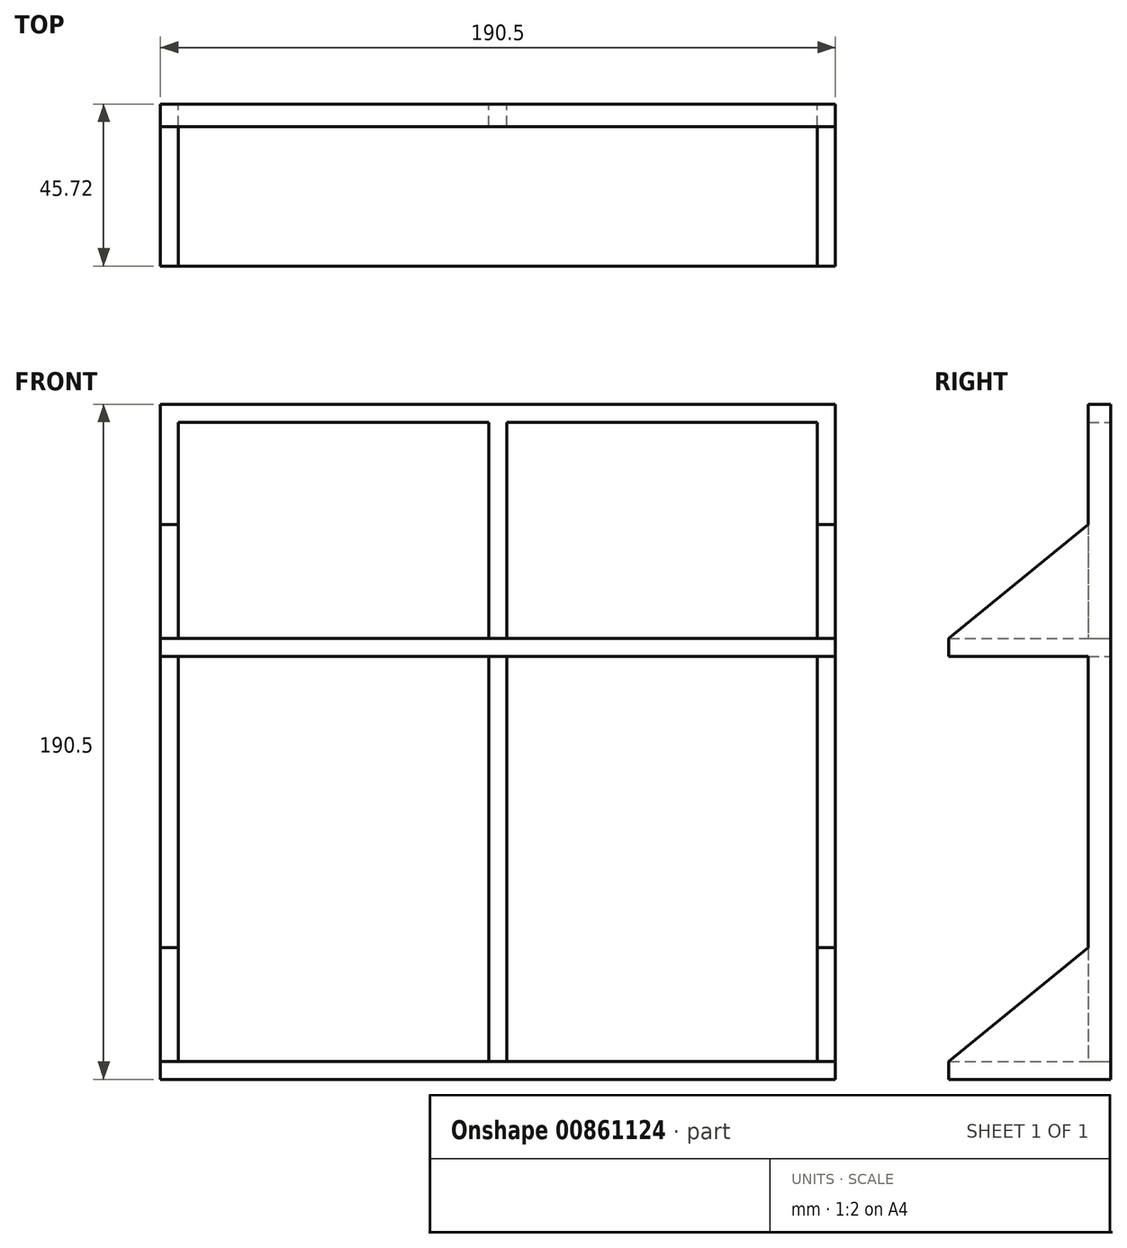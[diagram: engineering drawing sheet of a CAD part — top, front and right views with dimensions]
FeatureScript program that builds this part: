
annotation { "Feature Type Name" : "Feature", "Feature Type Description" : "" }
export const myFeature = defineFeature(function(context is Context, id is Id, definition is map)
    precondition{}
    {
        {
            var Q0;
            Q0=qCreatedBy(makeId("Front.planeOp"),FACE);
            var sketch = newSketch(context, id + "F0", { "sketchPlane" : qUnion([Q0])});
            skLineSegment(sketch, "E0.bottom", {"start": v(-95.25, 95.25) * mm, "end": v(95.25, 95.25) * mm});
            skLineSegment(sketch, "E0.top", {"start": v(-95.25, -95.25) * mm, "end": v(95.25, -95.25) * mm});
            skLineSegment(sketch, "E0.left", {"start": v(-95.25, 95.25) * mm, "end": v(-95.25, -95.25) * mm});
            skLineSegment(sketch, "E0.right", {"start": v(95.25, 95.25) * mm, "end": v(95.25, -95.25) * mm});
            skPoint(sketch, "E0.middle", {"position": v(0, 0) * mm});
            skLineSegment(sketch, "E1", {"start": v(90.17, 90.17) * mm, "end": v(2.54, 90.17) * mm});
            skLineSegment(sketch, "E2", {"start": v(-95.25, -90.17) * mm, "end": v(-2.54, -90.17) * mm});
            skLineSegment(sketch, "E3", {"start": v(-90.17, 90.17) * mm, "end": v(-90.17, 29.2) * mm});
            skLineSegment(sketch, "E4", {"start": v(90.17, 90.17) * mm, "end": v(90.17, 29.2) * mm});
            skLineSegment(sketch, "E5", {"start": v(-95.25, 24.13) * mm, "end": v(95.25, 24.13) * mm});
            skLineSegment(sketch, "E6", {"start": v(-95.25, 29.2) * mm, "end": v(95.25, 29.2) * mm});
            skPoint(sketch, "E7.orphan", {"position": v(-90.17, -95.25) * mm});
            skPoint(sketch, "E8.orphan", {"position": v(90.17, -95.25) * mm});
            skPoint(sketch, "E9.orphan", {"position": v(95.25, 90.17) * mm});
            skLineSegment(sketch, "E10.trimOffspring", {"start": v(90.17, 24.13) * mm, "end": v(90.17, -90.17) * mm});
            skLineSegment(sketch, "E11.trimOffspring", {"start": v(-90.17, 24.13) * mm, "end": v(-90.17, -90.17) * mm});
            skLineSegment(sketch, "E12", {"start": v(2.54, 90.17) * mm, "end": v(2.54, 29.2) * mm});
            skLineSegment(sketch, "E13", {"start": v(-2.54, 90.17) * mm, "end": v(-2.54, 29.2) * mm});
            skLineSegment(sketch, "E14.trimOffspring", {"start": v(2.54, -90.17) * mm, "end": v(95.25, -90.17) * mm});
            skPoint(sketch, "E15.orphan", {"position": v(0, -90.17) * mm});
            skLineSegment(sketch, "E16.trimOffspring", {"start": v(-2.54, 90.17) * mm, "end": v(-90.17, 90.17) * mm});
            skLineSegment(sketch, "E17.trimOffspring", {"start": v(2.54, 24.13) * mm, "end": v(2.54, -90.17) * mm});
            skLineSegment(sketch, "E18.trimOffspring", {"start": v(-2.54, 24.13) * mm, "end": v(-2.54, -90.17) * mm});
            skLineSegment(sketch, "E19", {"start": v(-2.54, -90.17) * mm, "end": v(2.54, -90.17) * mm});
            skPoint(sketch, "E20.start.orphan", {"position": v(0, 90.17) * mm});
            skSolve(sketch);
        }
        {
            var Q0;
            {var subQ4=sQuery(id+"F0.wireOp",EDGE,"E0.left");var subQ6=sQuery(id+"F0.wireOp",EDGE,"E5");var subQ12=makeQuery(id+"F0.imprint","INTERSECT",VERTEX,{"derivedFrom":[subQ4,subQ6]});Q0=makeQuery(id+"F0.imprint","IMPRINT",FACE,{"disambiguationData":[TD([[makeQuery(id+"F0.imprint","IMPRINT",EDGE,{"disambiguationData":[TD([[subQ12,1.0]])],"derivedFrom":subQ4}),1.0]])]});}
            var Q1;
            {var subQ1=sQuery(id+"F0.wireOp",EDGE,"E0.top");Q1=makeQuery(id+"F0.imprint","IMPRINT",FACE,{"disambiguationData":[TD([[makeQuery(id+"F0.imprint","IMPRINT",EDGE,{"derivedFrom":subQ1}),1.0]])]});}
            extrude(context, id + "F1", {"entities" : qUnion([Q0, Q1]), "depth" : 45.72 * mm, "offsetDistance" : 25.4 * mm});
        }
        {
            var Q0;
            {var subQ5=sQuery(id+"F0.wireOp",EDGE,"E11.trimOffspring");Q0=makeQuery(id+"F0.imprint","IMPRINT",FACE,{"disambiguationData":[TD([[makeQuery(id+"F0.imprint","IMPRINT",EDGE,{"derivedFrom":subQ5}),-1.0]])]});}
            var Q1;
            {var subQ7=sQuery(id+"F0.wireOp",EDGE,"E0.bottom");Q1=makeQuery(id+"F0.imprint","IMPRINT",FACE,{"disambiguationData":[TD([[makeQuery(id+"F0.imprint","IMPRINT",EDGE,{"derivedFrom":subQ7}),-1.0]])]});}
            var Q2;
            {var subQ0=sQuery(id+"F0.wireOp",EDGE,"E17.trimOffspring");Q2=makeQuery(id+"F0.imprint","IMPRINT",FACE,{"disambiguationData":[TD([[makeQuery(id+"F0.imprint","IMPRINT",EDGE,{"derivedFrom":subQ0}),-1.0]])]});}
            var Q3;
            {var subQ5=sQuery(id+"F0.wireOp",EDGE,"E10.trimOffspring");Q3=makeQuery(id+"F0.imprint","IMPRINT",FACE,{"disambiguationData":[TD([[makeQuery(id+"F0.imprint","IMPRINT",EDGE,{"derivedFrom":subQ5}),1.0]])]});}
            extrude(context, id + "F2", {"entities" : qUnion([Q0, Q1, Q2, Q3]), "depth" : 6.35 * mm, "offsetDistance" : 25.4 * mm});
        }
        {
            var Q0;
            Q0=makeQuery(id+"F1.opExtrude","SWEPT_BODY",BODY,{"disambiguationData":[OSD([sQuery(id+"F0.wireOp",EDGE,"E0.top"),sQuery(id+"F0.wireOp",EDGE,"E0.left"),sQuery(id+"F0.wireOp",EDGE,"E0.right"),sQuery(id+"F0.wireOp",EDGE,"E2"),sQuery(id+"F0.wireOp",EDGE,"E14.trimOffspring"),sQuery(id+"F0.wireOp",EDGE,"E19")])]});
            var Q1;
            Q1=makeQuery(id+"F1.opExtrude","SWEPT_BODY",BODY,{"disambiguationData":[OSD([sQuery(id+"F0.wireOp",EDGE,"E0.left"),sQuery(id+"F0.wireOp",EDGE,"E0.right"),sQuery(id+"F0.wireOp",EDGE,"E5"),sQuery(id+"F0.wireOp",EDGE,"E6")])]});
            var Q2;
            Q2=makeQuery(id+"F2.opExtrude","SWEPT_BODY",BODY,{"disambiguationData":[OSD([sQuery(id+"F0.wireOp",EDGE,"E0.bottom"),sQuery(id+"F0.wireOp",EDGE,"E0.left"),sQuery(id+"F0.wireOp",EDGE,"E0.right"),sQuery(id+"F0.wireOp",EDGE,"E1"),sQuery(id+"F0.wireOp",EDGE,"E3"),sQuery(id+"F0.wireOp",EDGE,"E4"),sQuery(id+"F0.wireOp",EDGE,"E6"),sQuery(id+"F0.wireOp",EDGE,"E12"),sQuery(id+"F0.wireOp",EDGE,"E13"),sQuery(id+"F0.wireOp",EDGE,"E16.trimOffspring")])]});
            var Q3;
            Q3=makeQuery(id+"F2.opExtrude","SWEPT_BODY",BODY,{"disambiguationData":[OSD([sQuery(id+"F0.wireOp",EDGE,"E0.left"),sQuery(id+"F0.wireOp",EDGE,"E2"),sQuery(id+"F0.wireOp",EDGE,"E5"),sQuery(id+"F0.wireOp",EDGE,"E11.trimOffspring")])]});
            var Q4;
            Q4=makeQuery(id+"F2.opExtrude","SWEPT_BODY",BODY,{"disambiguationData":[OSD([sQuery(id+"F0.wireOp",EDGE,"E0.right"),sQuery(id+"F0.wireOp",EDGE,"E5"),sQuery(id+"F0.wireOp",EDGE,"E10.trimOffspring"),sQuery(id+"F0.wireOp",EDGE,"E14.trimOffspring")])]});
            var Q5;
            Q5=makeQuery(id+"F2.opExtrude","SWEPT_BODY",BODY,{"disambiguationData":[OSD([sQuery(id+"F0.wireOp",EDGE,"E5"),sQuery(id+"F0.wireOp",EDGE,"E17.trimOffspring"),sQuery(id+"F0.wireOp",EDGE,"E18.trimOffspring"),sQuery(id+"F0.wireOp",EDGE,"E19")])]});
            booleanBodies(context, id + "F3", {"operationType" : BooleanOperationType.UNION, "tools" : qUnion([Q0, Q1, Q2, Q3, Q4, Q5])});
        }
        {
            var Q0;
            {var subQ0=sQuery(id+"F0.wireOp",EDGE,"E0.right");var subQ1=makeQuery(id+"F0.imprint","INTERSECT",VERTEX,{"derivedFrom":[subQ0,sQuery(id+"F0.wireOp",EDGE,"E5")]});Q0=makeQuery(id+"F3.opBoolean","MERGE",FACE,{"derivedFrom":[makeQuery(id+"F1.opExtrude","SWEPT_FACE",FACE,{"disambiguationData":[OSD([subQ0]),TDD([makeQuery(id+"F0.imprint","IMPRINT",EDGE,{"disambiguationData":[TD([[subQ1,1.0]])],"derivedFrom":subQ0})])]}),makeQuery(id+"F1.opExtrude","SWEPT_FACE",FACE,{"disambiguationData":[OSD([subQ0]),TDD([makeQuery(id+"F0.imprint","IMPRINT",EDGE,{"disambiguationData":[TD([[makeQuery(id+"F0.imprint","INTERSECT",VERTEX,{"derivedFrom":[sQuery(id+"F0.wireOp",EDGE,"E0.top"),subQ0]}),1.0]])],"derivedFrom":subQ0})])]}),makeQuery(id+"F2.opExtrude","SWEPT_FACE",FACE,{"disambiguationData":[OSD([subQ0]),TDD([makeQuery(id+"F0.imprint","IMPRINT",EDGE,{"disambiguationData":[TD([[makeQuery(id+"F0.imprint","INTERSECT",VERTEX,{"derivedFrom":[sQuery(id+"F0.wireOp",EDGE,"E0.bottom"),subQ0]}),-1.0]])],"derivedFrom":subQ0})])]}),makeQuery(id+"F2.opExtrude","SWEPT_FACE",FACE,{"disambiguationData":[OSD([subQ0]),TDD([makeQuery(id+"F0.imprint","IMPRINT",EDGE,{"disambiguationData":[TD([[subQ1,-1.0]])],"derivedFrom":subQ0})])]})]});}
            var sketch = newSketch(context, id + "F4", { "sketchPlane" : qUnion([Q0])});
            skLineSegment(sketch, "E21", {"start": v(-45.72, 29.21) * mm, "end": v(-6.35, 61.31) * mm});
            skLineSegment(sketch, "E22", {"start": v(-45.72, -90.17) * mm, "end": v(-6.35, -58.07) * mm});
            skSolve(sketch);
        }
        {
            var Q0;
            {var subQ0=sQuery(id+"F4.wireOp",EDGE,"E21");Q0=makeQuery(id+"F4.imprint","IMPRINT",FACE,{"disambiguationData":[TD([[makeQuery(id+"F4.imprint","IMPRINT",EDGE,{"derivedFrom":subQ0}),-1.0]])]});}
            var Q1;
            {var subQ0=sQuery(id+"F4.wireOp",EDGE,"E22");Q1=makeQuery(id+"F4.imprint","IMPRINT",FACE,{"disambiguationData":[TD([[makeQuery(id+"F4.imprint","IMPRINT",EDGE,{"derivedFrom":subQ0}),-1.0]])]});}
            extrude(context, id + "F5", {"entities" : qUnion([Q0, Q1]), "operationType" : NewBodyOperationType.ADD, "depth" : -5.08 * mm, "offsetDistance" : 25.4 * mm});
        }
        {
            var Q0;
            {var subQ0=sQuery(id+"F0.wireOp",EDGE,"E0.left");var subQ1=makeQuery(id+"F0.imprint","INTERSECT",VERTEX,{"derivedFrom":[subQ0,sQuery(id+"F0.wireOp",EDGE,"E2")]});var subQ2=makeQuery(id+"F0.imprint","INTERSECT",VERTEX,{"derivedFrom":[subQ0,sQuery(id+"F0.wireOp",EDGE,"E5")]});Q0=makeQuery(id+"F3.opBoolean","MERGE",FACE,{"derivedFrom":[makeQuery(id+"F1.opExtrude","SWEPT_FACE",FACE,{"disambiguationData":[OSD([subQ0]),TDD([makeQuery(id+"F0.imprint","IMPRINT",EDGE,{"disambiguationData":[TD([[subQ2,1.0]])],"derivedFrom":subQ0})])]}),makeQuery(id+"F1.opExtrude","SWEPT_FACE",FACE,{"disambiguationData":[OSD([subQ0]),TDD([makeQuery(id+"F0.imprint","IMPRINT",EDGE,{"disambiguationData":[TD([[makeQuery(id+"F0.imprint","INTERSECT",VERTEX,{"derivedFrom":[sQuery(id+"F0.wireOp",EDGE,"E0.top"),subQ0]}),1.0]])],"derivedFrom":subQ0})])]}),makeQuery(id+"F2.opExtrude","SWEPT_FACE",FACE,{"disambiguationData":[OSD([subQ0]),TDD([makeQuery(id+"F0.imprint","IMPRINT",EDGE,{"disambiguationData":[TD([[makeQuery(id+"F0.imprint","INTERSECT",VERTEX,{"derivedFrom":[sQuery(id+"F0.wireOp",EDGE,"E0.bottom"),subQ0]}),-1.0]])],"derivedFrom":subQ0})])]}),makeQuery(id+"F2.opExtrude","SWEPT_FACE",FACE,{"disambiguationData":[OSD([subQ0]),TDD([makeQuery(id+"F0.imprint","IMPRINT",EDGE,{"disambiguationData":[TD([[subQ1,1.0]])],"derivedFrom":subQ0})])]})]});}
            var sketch = newSketch(context, id + "F6", { "sketchPlane" : qUnion([Q0])});
            skLineSegment(sketch, "E23", {"start": v(45.72, 29.2) * mm, "end": v(6.35, 61.31) * mm});
            skLineSegment(sketch, "E24", {"start": v(45.72, -90.17) * mm, "end": v(6.35, -58.07) * mm});
            skSolve(sketch);
        }
        {
            var Q0;
            {var subQ0=sQuery(id+"F6.wireOp",EDGE,"E23");Q0=makeQuery(id+"F6.imprint","IMPRINT",FACE,{"disambiguationData":[TD([[makeQuery(id+"F6.imprint","IMPRINT",EDGE,{"derivedFrom":subQ0}),1.0]])]});}
            var Q1;
            {var subQ0=sQuery(id+"F6.wireOp",EDGE,"E24");Q1=makeQuery(id+"F6.imprint","IMPRINT",FACE,{"disambiguationData":[TD([[makeQuery(id+"F6.imprint","IMPRINT",EDGE,{"derivedFrom":subQ0}),1.0]])]});}
            extrude(context, id + "F7", {"entities" : qUnion([Q0, Q1]), "operationType" : NewBodyOperationType.ADD, "depth" : -5.08 * mm, "offsetDistance" : 25.4 * mm});
        }
    });
